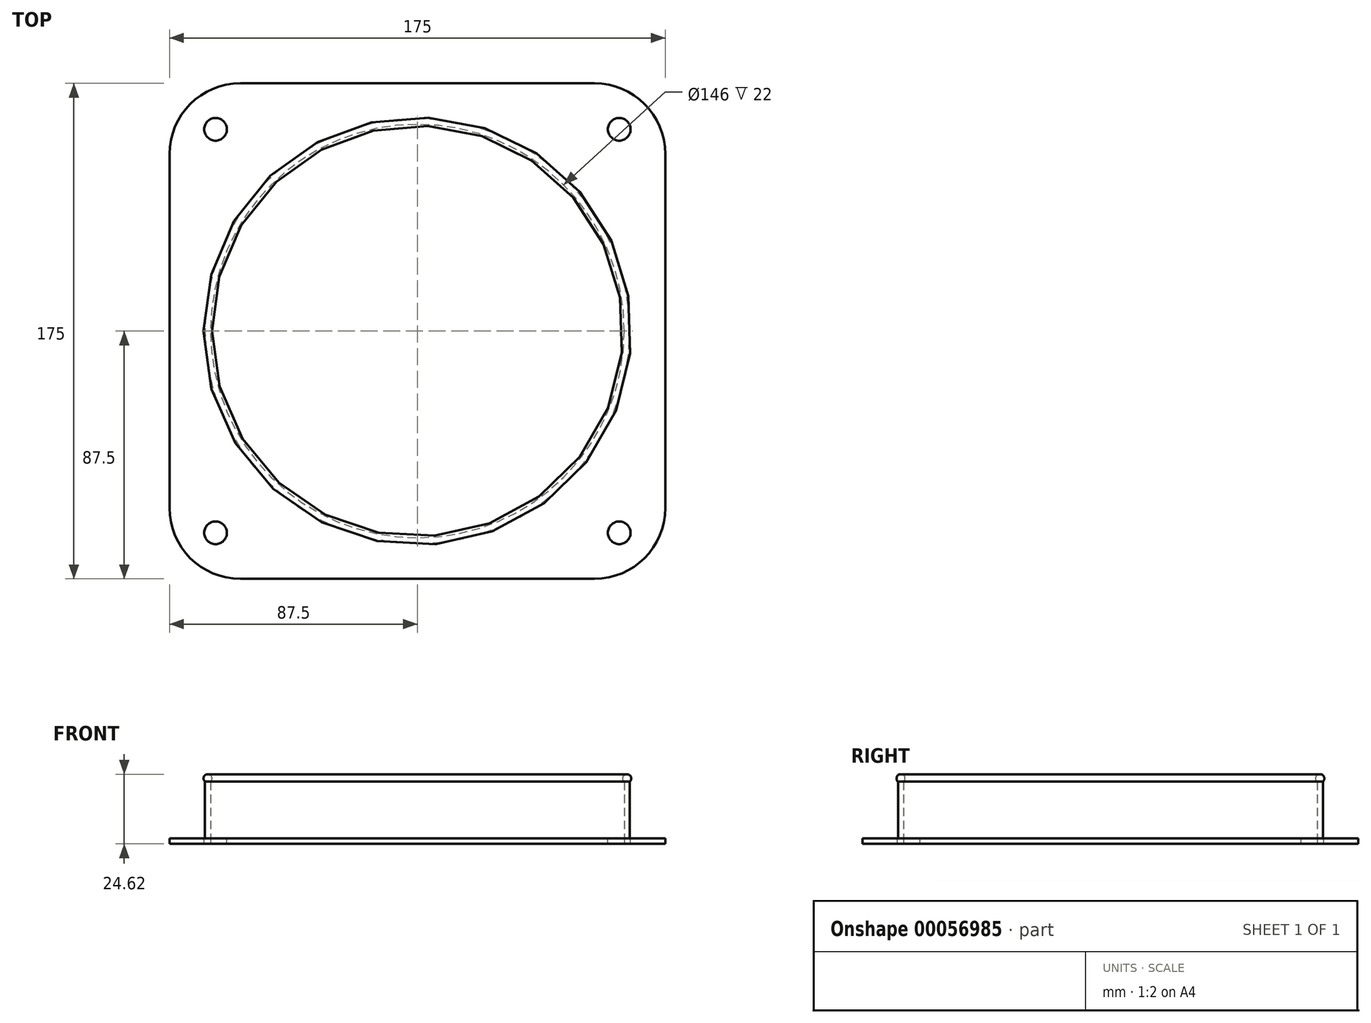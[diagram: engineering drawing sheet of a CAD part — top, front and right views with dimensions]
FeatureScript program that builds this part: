
annotation { "Feature Type Name" : "Feature", "Feature Type Description" : "" }
export const myFeature = defineFeature(function(context is Context, id is Id, definition is map)
    precondition{}
    {
        {
            var Q0;
            Q0=qCreatedBy(makeId("Top.planeOp"),FACE);
            var sketch = newSketch(context, id + "F0", { "sketchPlane" : qUnion([Q0])});
            skLineSegment(sketch, "E0.rect.bottom", {"start": v(87.5, -87.5) * mm, "end": v(-87.5, -87.5) * mm});
            skLineSegment(sketch, "E0.rect.top", {"start": v(87.5, 87.5) * mm, "end": v(-87.5, 87.5) * mm});
            skLineSegment(sketch, "E0.rect.left", {"start": v(87.5, -87.5) * mm, "end": v(87.5, 87.5) * mm});
            skLineSegment(sketch, "E0.rect.right", {"start": v(-87.5, -87.5) * mm, "end": v(-87.5, 87.5) * mm});
            skPoint(sketch, "E0.rect.middle", {"position": v(0, 0) * mm});
            skCircle(sketch, "E1", {"center": v(0, 0) * mm, "radius": 73 * mm});
            skSolve(sketch);
        }
        {
            var Q0;
            Q0=makeQuery(id+"F0.imprint","IMPRINT",FACE,{"disambiguationData":[TD([[makeQuery(id+"F0.imprint","IMPRINT",EDGE,{"derivedFrom":sQuery(id+"F0.wireOp",EDGE,"E0.rect.bottom")}),-1.0]])]});
            extrude(context, id + "F1", {"entities" : qUnion([Q0]), "depth" : 2 * mm});
        }
        {
            var Q0;
            Q0=makeQuery(id+"F1.opExtrude","CAP_FACE",FACE,{"disambiguationData":[OSD([sQuery(id+"F0.wireOp",EDGE,"E0.rect.bottom"),sQuery(id+"F0.wireOp",EDGE,"E0.rect.top"),sQuery(id+"F0.wireOp",EDGE,"E0.rect.left"),sQuery(id+"F0.wireOp",EDGE,"E0.rect.right"),sQuery(id+"F0.wireOp",EDGE,"E1")])],"isStart":false});
            var sketch = newSketch(context, id + "F2", { "sketchPlane" : qUnion([Q0])});
            skCircle(sketch, "E2", {"center": v(0, 0) * mm, "radius": 75 * mm});
            skSolve(sketch);
        }
        {
            var Q0;
            Q0=makeQuery(id+"F2.imprint","IMPRINT",FACE,{"disambiguationData":[TD([[makeQuery(id+"F2.imprint","IMPRINT",EDGE,{"derivedFrom":sQuery(id+"F2.wireOp",EDGE,"E2")}),1.0]])]});
            extrude(context, id + "F3", {"entities" : qUnion([Q0]), "operationType" : NewBodyOperationType.ADD, "depth" : 20 * mm});
        }
        {
            var Q0;
            Q0=qCreatedBy(makeId("Right.planeOp"),FACE);
            var sketch = newSketch(context, id + "F4", { "sketchPlane" : qUnion([Q0])});
            skLineSegment(sketch, "E3", {"start": v(75, 22) * mm, "end": v(75, 2) * mm});
            skLineSegment(sketch, "E4", {"start": v(-75, 2) * mm, "end": v(-75, 22) * mm});
            skLineSegment(sketch, "E5", {"start": v(73, 22) * mm, "end": v(73, 0) * mm});
            skLineSegment(sketch, "E6", {"start": v(-73, 0) * mm, "end": v(-73, 22) * mm});
            skLineSegment(sketch, "E7", {"start": v(-73, 22) * mm, "end": v(-75, 22) * mm});
            skLineSegment(sketch, "E8", {"start": v(75, 22) * mm, "end": v(73, 22) * mm});
            skCircle(sketch, "E9", {"center": v(-74, 23.12) * mm, "radius": 1.5 * mm});
            skPoint(sketch, "E9.centerSnap0", {"position": v(-74, 22) * mm});
            skLineSegment(sketch, "E10", {"start": v(0, 0) * mm, "end": v(0, 32.78) * mm});
            skSolve(sketch);
        }
        {
            var Q0;
            {var subQ0=sQuery(id+"F4.wireOp",EDGE,"E7");Q0=makeQuery(id+"F4.imprint","IMPRINT",FACE,{"disambiguationData":[TD([[makeQuery(id+"F4.imprint","IMPRINT",EDGE,{"derivedFrom":subQ0}),-1.0]])]});}
            var Q1;
            Q1=sQuery(id+"F4.wireOp",EDGE,"E10");
            revolve(context, id + "F5", {"entities" : qUnion([Q0]), "axis" : qUnion([Q1]), "revolveType" : RevolveType.FULL});
        }
        {
            var Q0;
            Q0=makeQuery(id+"F1.opExtrude","SWEPT_EDGE",EDGE,{"disambiguationData":[OSD([sQuery(id+"F0.wireOp",EDGE,"E0.rect.bottom"),sQuery(id+"F0.wireOp",EDGE,"E0.rect.right")])]});
            var Q1;
            Q1=makeQuery(id+"F1.opExtrude","SWEPT_EDGE",EDGE,{"disambiguationData":[OSD([sQuery(id+"F0.wireOp",EDGE,"E0.rect.bottom"),sQuery(id+"F0.wireOp",EDGE,"E0.rect.left")])]});
            var Q2;
            Q2=makeQuery(id+"F1.opExtrude","SWEPT_EDGE",EDGE,{"disambiguationData":[OSD([sQuery(id+"F0.wireOp",EDGE,"E0.rect.top"),sQuery(id+"F0.wireOp",EDGE,"E0.rect.left")])]});
            var Q3;
            Q3=makeQuery(id+"F1.opExtrude","SWEPT_EDGE",EDGE,{"disambiguationData":[OSD([sQuery(id+"F0.wireOp",EDGE,"E0.rect.top"),sQuery(id+"F0.wireOp",EDGE,"E0.rect.right")])]});
            fillet(context, id + "F6", {"entities" : qUnion([Q0, Q1, Q2, Q3]), "radius" : 25 * mm, "tangentPropagation" : true, "allowEdgeOverflow" : false});
        }
        {
            var Q0;
            Q0=makeQuery(id+"F1.opExtrude","CAP_FACE",FACE,{"disambiguationData":[OSD([sQuery(id+"F0.wireOp",EDGE,"E0.rect.bottom"),sQuery(id+"F0.wireOp",EDGE,"E0.rect.top"),sQuery(id+"F0.wireOp",EDGE,"E0.rect.left"),sQuery(id+"F0.wireOp",EDGE,"E0.rect.right"),sQuery(id+"F0.wireOp",EDGE,"E1")])],"isStart":false});
            var sketch = newSketch(context, id + "F7", { "sketchPlane" : qUnion([Q0])});
            skLineSegment(sketch, "E11.rect.bottom", {"start": v(-71.25, 71.25) * mm, "end": v(71.25, 71.25) * mm});
            skLineSegment(sketch, "E11.rect.top", {"start": v(-71.25, -71.25) * mm, "end": v(71.25, -71.25) * mm});
            skLineSegment(sketch, "E11.rect.left", {"start": v(-71.25, 71.25) * mm, "end": v(-71.25, -71.25) * mm});
            skLineSegment(sketch, "E11.rect.right", {"start": v(71.25, 71.25) * mm, "end": v(71.25, -71.25) * mm});
            skPoint(sketch, "E11.rect.middle", {"position": v(0, 0) * mm});
            skSolve(sketch);
        }
        {
            var Q0;
            Q0=sQuery(id+"F7.wireOp",VERTEX,"E11.rect.left.start");
            var Q1;
            Q1=sQuery(id+"F7.wireOp",VERTEX,"E11.rect.right.start");
            var Q2;
            Q2=sQuery(id+"F7.wireOp",VERTEX,"E11.rect.top.end");
            var Q3;
            Q3=sQuery(id+"F7.wireOp",VERTEX,"E11.rect.left.end");
            var Q4;
            Q4=makeQuery(id+"F1.opExtrude","SWEPT_BODY",BODY,{"disambiguationData":[OSD([sQuery(id+"F0.wireOp",EDGE,"E0.rect.bottom"),sQuery(id+"F0.wireOp",EDGE,"E0.rect.top"),sQuery(id+"F0.wireOp",EDGE,"E0.rect.left"),sQuery(id+"F0.wireOp",EDGE,"E0.rect.right"),sQuery(id+"F0.wireOp",EDGE,"E1")])]});
            hole(context, id + "F8", {"style" : HoleStyle.SIMPLE, "holeDiameter" : 8 * mm, "endStyle" : HoleEndStyle.THROUGH, "locations" : qUnion([Q0, Q1, Q2, Q3]), "scope" : qUnion([Q4])});
        }
    });
